# Revit family: Drain_Square_Top_9_Inch-Zurn-Z609-Heavy-Duty
name_source: partatom
category: Plumbing Fixtures
units: mm (PartAtom-declared; Revit-internal decimal feet)

## family parameters
Always vertical = Yes
Cut with Voids When Loaded = No
Maintain Annotation Orientation = No
OmniClass Number = 23.70.50.21.24.14
OmniClass Title = Deck Waste Water Drains
Part Type = Normal
Room Calculation Point = No
Round Connector Dimension = Use Radius
Shared = No
Work Plane-Based = No

## types (36) — shared parameters
Approx. Weight (Lbs) = 32 "
Assembly Code = D2030300
CW Connection = No
Default Elevation = 25 "
Description = 9 [229] SQUARE HEAVY-DUTY DRAIN
Grate Open Area Sq.in = 14 "
HW Connection = No
Main Material = Iron - Zurn - Cast - Painted - Blue
Manufacturer = Zurn Water, LLC
Manufacurer Brand = Zurn
Modified Date = 12/12/2025
Product Documentation Link = https://files.zurn.com
Product Page URL = https://www.zurn.com
Product data url = https://www.bimobject.com
Top Diameter Inner = 9 "
Top Diameter Width = 13.375 "
URL = www.zurn.com
Vent Connection = No
WFU = 1
Waste Connection = Yes
zero-valued in all types: CWFU, HWFU

## per-type parameters (varying)
| type | A_ Pipe Size (Actual-Inner) | A_ Pipe Size (Actual-Outer) | A_ Pipe Size (Nominal) | Body Height_E | Connector Radius | Frame And Grate | Frame Dimension | Model | Top Diameter | Type Comments | ZN-TOP |
| Z609-2IC | 2.067 " | 2.375 " | 2 " | 3.75 " | 1 " | Iron - Zurn - Cast - Painted - Blue | 2.438 " | Z609 | 9 " | Z609-2 Inch-Inside Caulk | No |
| Z609-2IP | 2.067 " | 2.375 " | 2 " | 2.75 " | 1 " | Iron - Zurn - Cast - Painted - Blue | 2.438 " | Z609 | 9 " | Z609-2 Inch-Threaded Outlet | No |
| Z609-2NH | 2.067 " | 2.375 " | 2 " | 4.75 " | 1 " | Iron - Zurn - Cast - Painted - Blue | 2.438 " | Z609 | 9 " | Z609-2 Inch-No Hub Outlet | No |
| Z609-2NL | 2.067 " | 2.375 " | 2 " | 3.5 " | 1 " | Iron - Zurn - Cast - Painted - Blue | 2.438 " | Z609 | 9 " | Z609-2 Inch-Neo Loc Outlet | No |
| Z609-3IC | 3.068 " | 3.5 " | 3 " | 3.75 " | 1.5 " | Iron - Zurn - Cast - Painted - Blue | 2.438 " | Z609 | 9 " | Z609-3 Inch-Inside Caulk | No |
| Z609-3IP | 3.068 " | 3.5 " | 3 " | 2.75 " | 1.5 " | Iron - Zurn - Cast - Painted - Blue | 2.438 " | Z609 | 9 " | Z609-3 Inch-Threaded Outlet | No |
| Z609-3NH | 3.068 " | 3.5 " | 3 " | 4.75 " | 1.5 " | Iron - Zurn - Cast - Painted - Blue | 2.438 " | Z609 | 9 " | Z609-3 Inch-No Hub Outlet | No |
| Z609-3NL | 3.068 " | 3.5 " | 3 " | 3.5 " | 1.5 " | Iron - Zurn - Cast - Painted - Blue | 2.438 " | Z609 | 9 " | Z609-3 Inch-Neo Loc Outlet | No |
| Z609-4IC | 4.026 " | 4.5 " | 4 " | 3.75 " | 2 " | Iron - Zurn - Cast - Painted - Blue | 2.438 " | Z609 | 9 " | Z609-4 Inch-Inside Caulk | No |
| Z609-4IP | 4.026 " | 4.5 " | 4 " | 2.75 " | 2 " | Iron - Zurn - Cast - Painted - Blue | 2.438 " | Z609 | 9 " | Z609-4 Inch-Threaded Outlet | No |
| Z609-4NH | 4.026 " | 4.5 " | 4 " | 4.75 " | 2 " | Iron - Zurn - Cast - Painted - Blue | 2.438 " | Z609 | 9 " | Z609-4 Inch-No Hub Outlet | No |
| Z609-4NL | 4.026 " | 4.5 " | 4 " | 3.5 " | 2 " | Iron - Zurn - Cast - Painted - Blue | 2.438 " | Z609 | 9 " | Z609-4 Inch-Neo Loc Outlet | No |
| ZB609-2IC | 2.067 " | 2.375 " | 2 " | 3.75 " | 1 " | Bronze - Zurn - Polished | 2.625 " | ZB609 | 9.75 " | ZB609-2 Inch-Inside Caulk | Yes |
| ZB609-2IP | 2.067 " | 2.375 " | 2 " | 2.75 " | 1 " | Bronze - Zurn - Polished | 2.625 " | ZB609 | 9.75 " | ZB609-2 Inch-Threaded Outlet | Yes |
| ZB609-2NH | 2.067 " | 2.375 " | 2 " | 4.75 " | 1 " | Bronze - Zurn - Polished | 2.625 " | ZB609 | 9.75 " | ZB609-2 Inch-No Hub Outlet | Yes |
| ZB609-2NL | 2.067 " | 2.375 " | 2 " | 3.5 " | 1 " | Bronze - Zurn - Polished | 2.625 " | ZB609 | 9.75 " | ZB609-2 Inch-Neo Loc Outlet | Yes |
| ZB609-3IC | 3.068 " | 3.5 " | 3 " | 3.75 " | 1.5 " | Bronze - Zurn - Polished | 2.625 " | ZB609 | 9.75 " | ZB609-3 Inch-Inside Caulk | Yes |
| ZB609-3IP | 3.068 " | 3.5 " | 3 " | 2.75 " | 1.5 " | Bronze - Zurn - Polished | 2.625 " | ZB609 | 9.75 " | ZB609-3 Inch-Threaded Outlet | Yes |
| ZB609-3NH | 3.068 " | 3.5 " | 3 " | 4.75 " | 1.5 " | Bronze - Zurn - Polished | 2.625 " | ZB609 | 9.75 " | ZB609-3 Inch-No Hub Outlet | Yes |
| ZB609-3NL | 3.068 " | 3.5 " | 3 " | 3.5 " | 1.5 " | Bronze - Zurn - Polished | 2.625 " | ZB609 | 9.75 " | ZB609-3 Inch-Neo Loc Outlet | Yes |
| ZB609-4IC | 4.026 " | 4.5 " | 4 " | 3.75 " | 2 " | Bronze - Zurn - Polished | 2.625 " | ZB609 | 9.75 " | ZB609-4 Inch-Inside Caulk | Yes |
| ZB609-4IP | 4.026 " | 4.5 " | 4 " | 2.75 " | 2 " | Bronze - Zurn - Polished | 2.625 " | ZB609 | 9.75 " | ZB609-4 Inch-Threaded Outlet | Yes |
| ZB609-4NH | 4.026 " | 4.5 " | 4 " | 4.75 " | 2 " | Bronze - Zurn - Polished | 2.625 " | ZB609 | 9.75 " | ZB609-4 Inch-No Hub Outlet | Yes |
| ZB609-4NL | 4.026 " | 4.5 " | 4 " | 3.5 " | 2 " | Bronze - Zurn - Polished | 2.625 " | ZB609 | 9.75 " | ZB609-4 Inch-Neo Loc Outlet | Yes |
| ZN609-2IC | 2.067 " | 2.375 " | 2 " | 3.75 " | 1 " | Bronze - Zurn - Polished Nickel | 2.625 " | ZN609 | 9.75 " | ZN609-2 Inch-Inside Caulk | Yes |
| ZN609-2IP | 2.067 " | 2.375 " | 2 " | 2.75 " | 1 " | Bronze - Zurn - Polished Nickel | 2.625 " | ZN609 | 9.75 " | ZN609-2 Inch-Threaded Outlet | Yes |
| ZN609-2NH | 2.067 " | 2.375 " | 2 " | 4.75 " | 1 " | Bronze - Zurn - Polished Nickel | 2.625 " | ZN609 | 9.75 " | ZN609-2 Inch-No Hub Outlet | Yes |
| ZN609-2NL | 2.067 " | 2.375 " | 2 " | 3.5 " | 1 " | Bronze - Zurn - Polished Nickel | 2.625 " | ZN609 | 9.75 " | ZN609-2 Inch-Neo Loc Outlet | Yes |
| ZN609-3IC | 3.068 " | 3.5 " | 3 " | 3.75 " | 1.5 " | Bronze - Zurn - Polished Nickel | 2.625 " | ZN609 | 9.75 " | ZN609-3 Inch-Inside Caulk | Yes |
| ZN609-3IP | 3.068 " | 3.5 " | 3 " | 2.75 " | 1.5 " | Bronze - Zurn - Polished Nickel | 2.625 " | ZN609 | 9.75 " | ZN609-3 Inch-Threaded Outlet | Yes |
| ZN609-3NH | 3.068 " | 3.5 " | 3 " | 4.75 " | 1.5 " | Bronze - Zurn - Polished Nickel | 2.625 " | ZN609 | 9.75 " | ZN609-3 Inch-No Hub Outlet | Yes |
| ZN609-3NL | 3.068 " | 3.5 " | 3 " | 3.5 " | 1.5 " | Bronze - Zurn - Polished Nickel | 2.625 " | ZN609 | 9.75 " | ZN609-3 Inch-Neo Loc Outlet | Yes |
| ZN609-4IC | 4.026 " | 4.5 " | 4 " | 3.75 " | 2 " | Bronze - Zurn - Polished Nickel | 2.625 " | ZN609 | 9.75 " | ZN609-4 Inch-Inside Caulk | Yes |
| ZN609-4IP | 4.026 " | 4.5 " | 4 " | 2.75 " | 2 " | Bronze - Zurn - Polished Nickel | 2.625 " | ZN609 | 9.75 " | ZN609-4 Inch-Threaded Outlet | Yes |
| ZN609-4NH | 4.026 " | 4.5 " | 4 " | 4.75 " | 2 " | Bronze - Zurn - Polished Nickel | 2.625 " | ZN609 | 9.75 " | ZN609-4 Inch-No Hub Outlet | Yes |
| ZN609-4NL | 4.026 " | 4.5 " | 4 " | 3.5 " | 2 " | Bronze - Zurn - Polished Nickel | 2.625 " | ZN609 | 9.75 " | ZN609-4 Inch-Neo Loc Outlet | Yes |

## geometry (parser evidence)
native form markers: Sweep x4
no freeform markers — native parametric forms only
